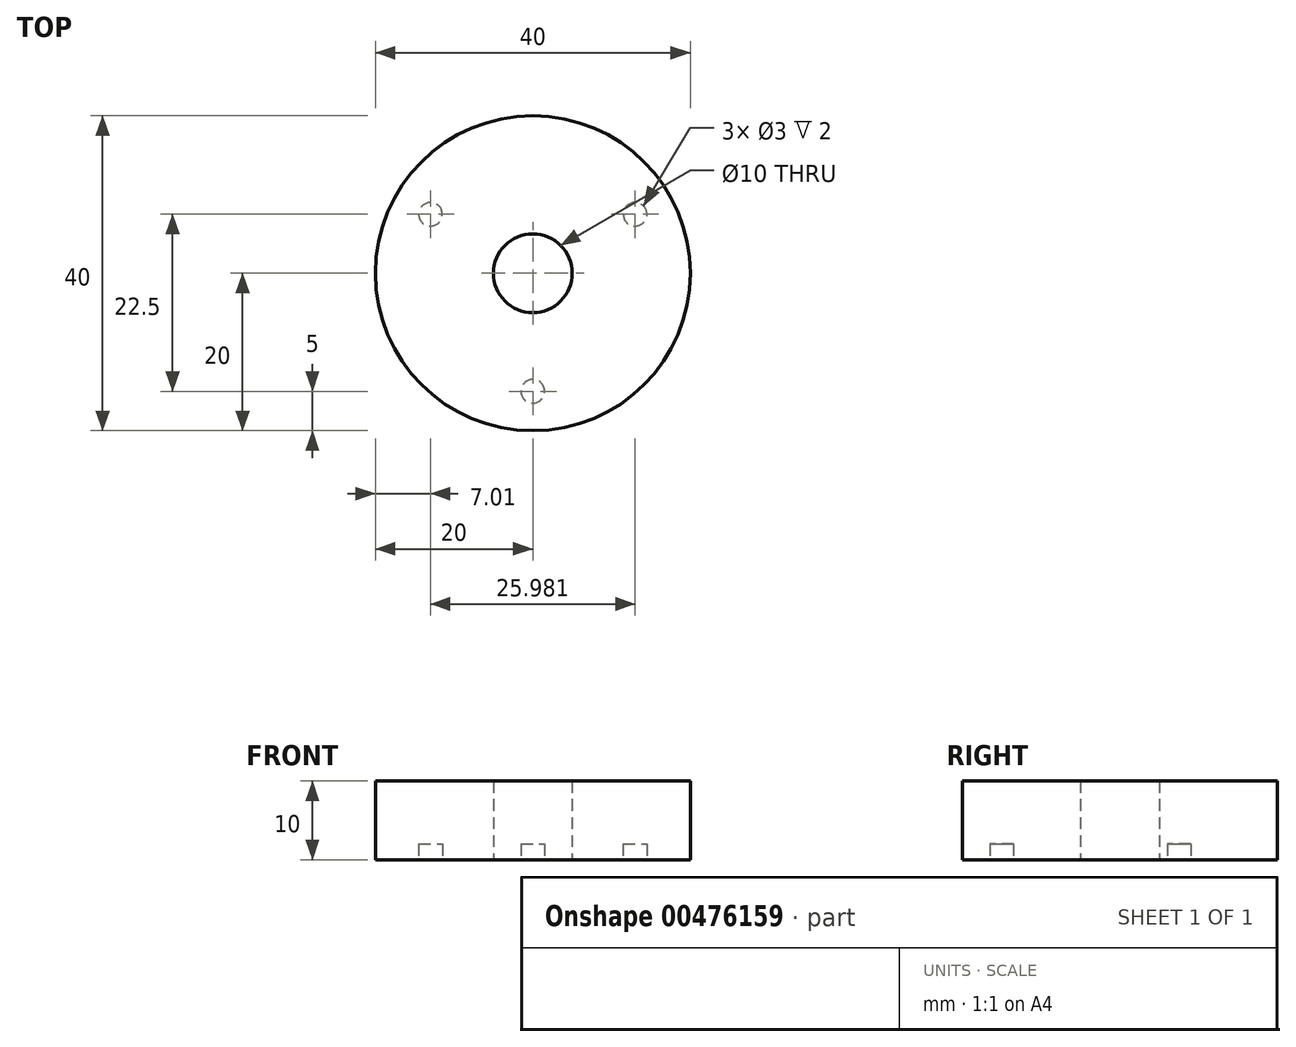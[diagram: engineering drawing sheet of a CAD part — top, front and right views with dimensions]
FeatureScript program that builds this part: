
annotation { "Feature Type Name" : "Feature", "Feature Type Description" : "" }
export const myFeature = defineFeature(function(context is Context, id is Id, definition is map)
    precondition{}
    {
        {
            var Q0;
            Q0=qCreatedBy(makeId("Top.planeOp"),FACE);
            var sketch = newSketch(context, id + "F0", { "sketchPlane" : qUnion([Q0])});
            skCircle(sketch, "E0", {"center": v(0, 0) * mm, "radius": 20 * mm});
            skCircle(sketch, "E1", {"center": v(0, 0) * mm, "radius": 5 * mm});
            skSolve(sketch);
        }
        {
            var Q0;
            Q0=qSketchRegion(id+"F0",true);
            extrude(context, id + "F1", {"entities" : qUnion([Q0]), "depth" : 10 * mm});
        }
        {
            var Q0;
            Q0=makeQuery(id+"F1.opExtrude","CAP_FACE",FACE,{"disambiguationData":[OSD([sQuery(id+"F0.wireOp",EDGE,"E0"),sQuery(id+"F0.wireOp",EDGE,"E1")])],"isStart":true});
            var sketch = newSketch(context, id + "F2", { "sketchPlane" : qUnion([Q0])});
            skCircle(sketch, "E2", {"center": v(0, 15) * mm, "radius": 1.5 * mm});
            skCircle(sketch, "E3.1.0", {"center": v(-13, -7.5) * mm, "radius": 1.5 * mm});
            skCircle(sketch, "E3.2.0", {"center": v(13, -7.5) * mm, "radius": 1.5 * mm});
            skPoint(sketch, "E3.center", {"position": v(0, 0) * mm});
            skSolve(sketch);
        }
        {
            var Q0;
            Q0=qSketchRegion(id+"F2",true);
            extrude(context, id + "F3", {"entities" : qUnion([Q0]), "operationType" : NewBodyOperationType.REMOVE, "oppositeDirection" : true, "depth" : 2 * mm});
        }
    });
